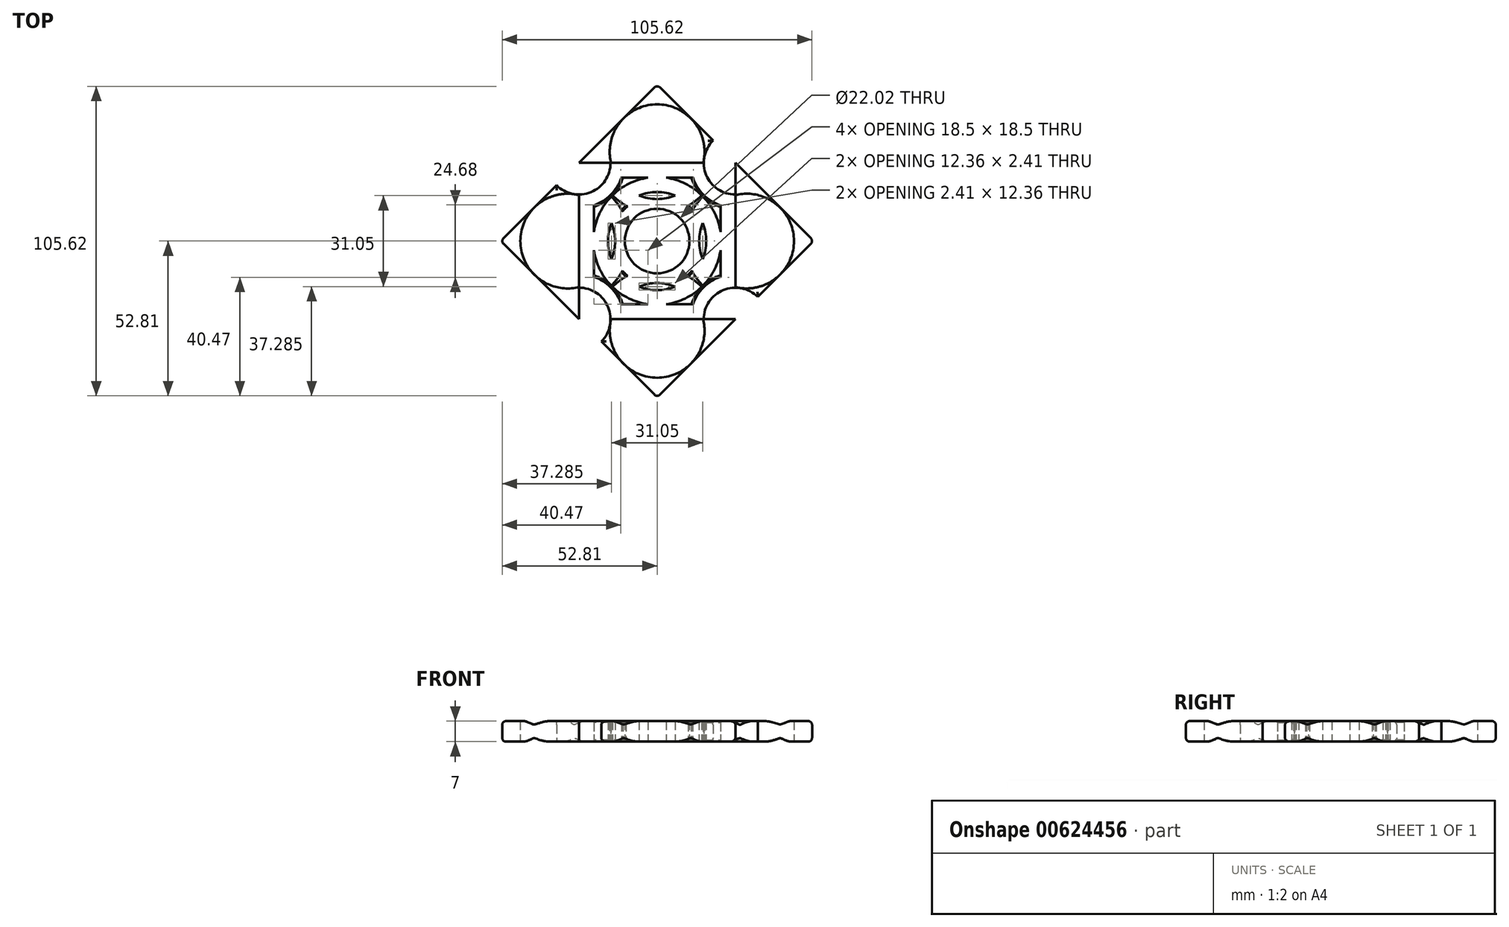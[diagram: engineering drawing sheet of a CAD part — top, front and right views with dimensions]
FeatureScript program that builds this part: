
annotation { "Feature Type Name" : "Feature", "Feature Type Description" : "" }
export const myFeature = defineFeature(function(context is Context, id is Id, definition is map)
    precondition{}
    {
        {
            var Q0;
            Q0=qCreatedBy(makeId("Top.planeOp"),FACE);
            var sketch = newSketch(context, id + "F0", { "sketchPlane" : qUnion([Q0])});
            skCircle(sketch, "E0", {"center": v(0, 0) * mm, "radius": 11.01 * mm});
            skLineSegment(sketch, "E1", {"start": v(0, 0) * mm, "end": v(0, 53.34) * mm});
            skLineSegment(sketch, "E2", {"start": v(0, 0) * mm, "end": v(53.34, 0) * mm});
            skLineSegment(sketch, "E3", {"start": v(0, 0) * mm, "end": v(-53.34, 0) * mm});
            skLineSegment(sketch, "E4", {"start": v(0, 0) * mm, "end": v(0, -53.34) * mm});
            skCircle(sketch, "E5", {"center": v(-30.48, 0) * mm, "radius": 11.01 * mm});
            skCircle(sketch, "E6", {"center": v(0, 30.48) * mm, "radius": 11.01 * mm});
            skCircle(sketch, "E7", {"center": v(30.48, 0) * mm, "radius": 11.01 * mm});
            skCircle(sketch, "E8", {"center": v(0, -30.48) * mm, "radius": 11.01 * mm});
            skLineSegment(sketch, "E9", {"start": v(0, 53.34) * mm, "end": v(-53.34, 0) * mm});
            skLineSegment(sketch, "E10", {"start": v(-53.34, 0) * mm, "end": v(0, -53.34) * mm});
            skLineSegment(sketch, "E11", {"start": v(0, -53.34) * mm, "end": v(53.34, 0) * mm});
            skLineSegment(sketch, "E12", {"start": v(53.34, 0) * mm, "end": v(0, 53.34) * mm});
            skCircle(sketch, "E13", {"center": v(26.67, -26.67) * mm, "radius": 10.78 * mm});
            skCircle(sketch, "E14", {"center": v(-26.67, -26.67) * mm, "radius": 10.78 * mm});
            skCircle(sketch, "E15", {"center": v(-26.67, 26.67) * mm, "radius": 10.78 * mm});
            skCircle(sketch, "E16", {"center": v(26.67, 26.67) * mm, "radius": 10.78 * mm});
            skLineSegment(sketch, "E17", {"start": v(0, 0) * mm, "end": v(-26.67, -26.67) * mm});
            skLineSegment(sketch, "E18", {"start": v(0, 0) * mm, "end": v(26.67, -26.67) * mm});
            skLineSegment(sketch, "E19", {"start": v(0, 0) * mm, "end": v(26.67, 26.67) * mm});
            skLineSegment(sketch, "E20", {"start": v(0, 0) * mm, "end": v(-26.67, 26.67) * mm});
            skLineSegment(sketch, "E21", {"start": v(26.67, 26.67) * mm, "end": v(26.67, -26.67) * mm});
            skLineSegment(sketch, "E22", {"start": v(-26.67, -26.67) * mm, "end": v(26.67, -26.67) * mm});
            skLineSegment(sketch, "E23", {"start": v(-26.67, -26.67) * mm, "end": v(-26.67, 26.67) * mm});
            skLineSegment(sketch, "E24", {"start": v(-26.67, 26.67) * mm, "end": v(26.67, 26.67) * mm});
            skCircle(sketch, "E25", {"center": v(-30.48, 0) * mm, "radius": 16.16 * mm});
            skCircle(sketch, "E26", {"center": v(0, 30.48) * mm, "radius": 16.16 * mm});
            skCircle(sketch, "E27", {"center": v(30.48, 0) * mm, "radius": 16.16 * mm});
            skCircle(sketch, "E28", {"center": v(0, -30.48) * mm, "radius": 16.16 * mm});
            skCircle(sketch, "E29", {"center": v(0, 0) * mm, "radius": 16.73 * mm});
            skSolve(sketch);
        }
        {
            var Q0;
            {var subQ0=sQuery(id+"F0.wireOp",EDGE,"E9");var subQ3=sQuery(id+"F0.wireOp",EDGE,"E26");var subQ5=makeQuery(id+"F0.imprint","INTERSECT",VERTEX,{"derivedFrom":[subQ0,subQ3]});Q0=makeQuery(id+"F0.imprint","IMPRINT",FACE,{"disambiguationData":[TD([[makeQuery(id+"F0.imprint","IMPRINT",EDGE,{"disambiguationData":[TD([[subQ5,1.0]])],"derivedFrom":subQ3}),-1.0]])]});}
            var Q1;
            {var subQ0=sQuery(id+"F0.wireOp",EDGE,"E12");var subQ3=sQuery(id+"F0.wireOp",EDGE,"E26");var subQ5=makeQuery(id+"F0.imprint","INTERSECT",VERTEX,{"derivedFrom":[subQ0,subQ3]});Q1=makeQuery(id+"F0.imprint","IMPRINT",FACE,{"disambiguationData":[TD([[makeQuery(id+"F0.imprint","IMPRINT",EDGE,{"disambiguationData":[TD([[subQ5,-1.0]])],"derivedFrom":subQ3}),-1.0]])]});}
            var Q2;
            {var subQ0=sQuery(id+"F0.wireOp",EDGE,"E11");var subQ3=sQuery(id+"F0.wireOp",EDGE,"E27");var subQ5=makeQuery(id+"F0.imprint","INTERSECT",VERTEX,{"derivedFrom":[subQ0,subQ3]});Q2=makeQuery(id+"F0.imprint","IMPRINT",FACE,{"disambiguationData":[TD([[makeQuery(id+"F0.imprint","IMPRINT",EDGE,{"disambiguationData":[TD([[subQ5,-1.0]])],"derivedFrom":subQ3}),-1.0]])]});}
            var Q3;
            {var subQ0=sQuery(id+"F0.wireOp",EDGE,"E12");var subQ3=sQuery(id+"F0.wireOp",EDGE,"E27");var subQ5=makeQuery(id+"F0.imprint","INTERSECT",VERTEX,{"derivedFrom":[subQ0,subQ3]});Q3=makeQuery(id+"F0.imprint","IMPRINT",FACE,{"disambiguationData":[TD([[makeQuery(id+"F0.imprint","IMPRINT",EDGE,{"disambiguationData":[TD([[subQ5,1.0]])],"derivedFrom":subQ3}),-1.0]])]});}
            var Q4;
            {var subQ0=sQuery(id+"F0.wireOp",EDGE,"E9");var subQ3=sQuery(id+"F0.wireOp",EDGE,"E25");var subQ5=makeQuery(id+"F0.imprint","INTERSECT",VERTEX,{"derivedFrom":[subQ0,subQ3]});Q4=makeQuery(id+"F0.imprint","IMPRINT",FACE,{"disambiguationData":[TD([[makeQuery(id+"F0.imprint","IMPRINT",EDGE,{"disambiguationData":[TD([[subQ5,-1.0]])],"derivedFrom":subQ3}),-1.0]])]});}
            var Q5;
            {var subQ0=sQuery(id+"F0.wireOp",EDGE,"E10");var subQ3=sQuery(id+"F0.wireOp",EDGE,"E25");var subQ5=makeQuery(id+"F0.imprint","INTERSECT",VERTEX,{"derivedFrom":[subQ0,subQ3]});Q5=makeQuery(id+"F0.imprint","IMPRINT",FACE,{"disambiguationData":[TD([[makeQuery(id+"F0.imprint","IMPRINT",EDGE,{"disambiguationData":[TD([[subQ5,1.0]])],"derivedFrom":subQ3}),-1.0]])]});}
            var Q6;
            {var subQ0=sQuery(id+"F0.wireOp",EDGE,"E10");var subQ3=sQuery(id+"F0.wireOp",EDGE,"E28");var subQ5=makeQuery(id+"F0.imprint","INTERSECT",VERTEX,{"derivedFrom":[subQ0,subQ3]});Q6=makeQuery(id+"F0.imprint","IMPRINT",FACE,{"disambiguationData":[TD([[makeQuery(id+"F0.imprint","IMPRINT",EDGE,{"disambiguationData":[TD([[subQ5,-1.0]])],"derivedFrom":subQ3}),-1.0]])]});}
            var Q7;
            {var subQ0=sQuery(id+"F0.wireOp",EDGE,"E11");var subQ3=sQuery(id+"F0.wireOp",EDGE,"E28");var subQ5=makeQuery(id+"F0.imprint","INTERSECT",VERTEX,{"derivedFrom":[subQ0,subQ3]});Q7=makeQuery(id+"F0.imprint","IMPRINT",FACE,{"disambiguationData":[TD([[makeQuery(id+"F0.imprint","IMPRINT",EDGE,{"disambiguationData":[TD([[subQ5,1.0]])],"derivedFrom":subQ3}),-1.0]])]});}
            var Q8;
            {var subQ0=sQuery(id+"F0.wireOp",EDGE,"E26");var subQ1=sQuery(id+"F0.wireOp",EDGE,"E9");var subQ2=makeQuery(id+"F0.imprint","INTERSECT",VERTEX,{"derivedFrom":[subQ1,subQ0]});Q8=makeQuery(id+"F0.imprint","IMPRINT",FACE,{"disambiguationData":[TD([[makeQuery(id+"F0.imprint","IMPRINT",EDGE,{"disambiguationData":[TD([[subQ2,-1.0]])],"derivedFrom":subQ1}),1.0]])]});}
            var Q9;
            {var subQ0=sQuery(id+"F0.wireOp",EDGE,"E15");var subQ1=sQuery(id+"F0.wireOp",EDGE,"E9");var subQ2=makeQuery(id+"F0.imprint","INTERSECT",VERTEX,{"disambiguationData":[OD(1.0)],"derivedFrom":[subQ1,subQ0]});Q9=makeQuery(id+"F0.imprint","IMPRINT",FACE,{"disambiguationData":[TD([[makeQuery(id+"F0.imprint","IMPRINT",EDGE,{"disambiguationData":[TD([[subQ2,-1.0]])],"derivedFrom":subQ1}),1.0]])]});}
            var Q10;
            {var subQ0=sQuery(id+"F0.wireOp",EDGE,"E25");var subQ1=sQuery(id+"F0.wireOp",EDGE,"E10");var subQ2=makeQuery(id+"F0.imprint","INTERSECT",VERTEX,{"derivedFrom":[subQ1,subQ0]});Q10=makeQuery(id+"F0.imprint","IMPRINT",FACE,{"disambiguationData":[TD([[makeQuery(id+"F0.imprint","IMPRINT",EDGE,{"disambiguationData":[TD([[subQ2,-1.0]])],"derivedFrom":subQ1}),1.0]])]});}
            var Q11;
            {var subQ0=sQuery(id+"F0.wireOp",EDGE,"E14");var subQ1=sQuery(id+"F0.wireOp",EDGE,"E10");var subQ2=makeQuery(id+"F0.imprint","INTERSECT",VERTEX,{"disambiguationData":[OD(1.0)],"derivedFrom":[subQ1,subQ0]});Q11=makeQuery(id+"F0.imprint","IMPRINT",FACE,{"disambiguationData":[TD([[makeQuery(id+"F0.imprint","IMPRINT",EDGE,{"disambiguationData":[TD([[subQ2,-1.0]])],"derivedFrom":subQ1}),1.0]])]});}
            var Q12;
            {var subQ0=sQuery(id+"F0.wireOp",EDGE,"E28");var subQ1=sQuery(id+"F0.wireOp",EDGE,"E11");var subQ2=makeQuery(id+"F0.imprint","INTERSECT",VERTEX,{"derivedFrom":[subQ1,subQ0]});Q12=makeQuery(id+"F0.imprint","IMPRINT",FACE,{"disambiguationData":[TD([[makeQuery(id+"F0.imprint","IMPRINT",EDGE,{"disambiguationData":[TD([[subQ2,-1.0]])],"derivedFrom":subQ1}),1.0]])]});}
            var Q13;
            {var subQ0=sQuery(id+"F0.wireOp",EDGE,"E13");var subQ1=sQuery(id+"F0.wireOp",EDGE,"E11");var subQ2=makeQuery(id+"F0.imprint","INTERSECT",VERTEX,{"disambiguationData":[OD(1.0)],"derivedFrom":[subQ1,subQ0]});Q13=makeQuery(id+"F0.imprint","IMPRINT",FACE,{"disambiguationData":[TD([[makeQuery(id+"F0.imprint","IMPRINT",EDGE,{"disambiguationData":[TD([[subQ2,-1.0]])],"derivedFrom":subQ1}),1.0]])]});}
            var Q14;
            {var subQ0=sQuery(id+"F0.wireOp",EDGE,"E27");var subQ1=sQuery(id+"F0.wireOp",EDGE,"E12");var subQ2=makeQuery(id+"F0.imprint","INTERSECT",VERTEX,{"derivedFrom":[subQ1,subQ0]});Q14=makeQuery(id+"F0.imprint","IMPRINT",FACE,{"disambiguationData":[TD([[makeQuery(id+"F0.imprint","IMPRINT",EDGE,{"disambiguationData":[TD([[subQ2,-1.0]])],"derivedFrom":subQ1}),1.0]])]});}
            var Q15;
            {var subQ0=sQuery(id+"F0.wireOp",EDGE,"E16");var subQ1=sQuery(id+"F0.wireOp",EDGE,"E12");var subQ2=makeQuery(id+"F0.imprint","INTERSECT",VERTEX,{"disambiguationData":[OD(1.0)],"derivedFrom":[subQ1,subQ0]});Q15=makeQuery(id+"F0.imprint","IMPRINT",FACE,{"disambiguationData":[TD([[makeQuery(id+"F0.imprint","IMPRINT",EDGE,{"disambiguationData":[TD([[subQ2,-1.0]])],"derivedFrom":subQ1}),1.0]])]});}
            var Q16;
            {var subQ2=sQuery(id+"F0.wireOp",EDGE,"E1");var subQ4=sQuery(id+"F0.wireOp",EDGE,"E6");var subQ5=makeQuery(id+"F0.imprint","INTERSECT",VERTEX,{"disambiguationData":[OD(1.0)],"derivedFrom":[subQ2,subQ4]});Q16=makeQuery(id+"F0.imprint","IMPRINT",FACE,{"disambiguationData":[TD([[makeQuery(id+"F0.imprint","IMPRINT",EDGE,{"disambiguationData":[TD([[subQ5,-1.0]])],"derivedFrom":subQ2}),1.0]])]});}
            var Q17;
            {var subQ2=sQuery(id+"F0.wireOp",EDGE,"E1");var subQ5=sQuery(id+"F0.wireOp",EDGE,"E6");var subQ8=makeQuery(id+"F0.imprint","INTERSECT",VERTEX,{"disambiguationData":[OD(1.0)],"derivedFrom":[subQ2,subQ5]});Q17=makeQuery(id+"F0.imprint","IMPRINT",FACE,{"disambiguationData":[TD([[makeQuery(id+"F0.imprint","IMPRINT",EDGE,{"disambiguationData":[TD([[subQ8,-1.0]])],"derivedFrom":subQ2}),-1.0]])]});}
            var Q18;
            {var subQ2=sQuery(id+"F0.wireOp",EDGE,"E2");var subQ5=sQuery(id+"F0.wireOp",EDGE,"E7");var subQ8=makeQuery(id+"F0.imprint","INTERSECT",VERTEX,{"disambiguationData":[OD(1.0)],"derivedFrom":[subQ2,subQ5]});Q18=makeQuery(id+"F0.imprint","IMPRINT",FACE,{"disambiguationData":[TD([[makeQuery(id+"F0.imprint","IMPRINT",EDGE,{"disambiguationData":[TD([[subQ8,-1.0]])],"derivedFrom":subQ2}),1.0]])]});}
            var Q19;
            {var subQ4=sQuery(id+"F0.wireOp",EDGE,"E7");var subQ6=sQuery(id+"F0.wireOp",EDGE,"E2");var subQ7=makeQuery(id+"F0.imprint","INTERSECT",VERTEX,{"disambiguationData":[OD(1.0)],"derivedFrom":[subQ6,subQ4]});Q19=makeQuery(id+"F0.imprint","IMPRINT",FACE,{"disambiguationData":[TD([[makeQuery(id+"F0.imprint","IMPRINT",EDGE,{"disambiguationData":[TD([[subQ7,-1.0]])],"derivedFrom":subQ6}),-1.0]])]});}
            var Q20;
            {var subQ1=sQuery(id+"F0.wireOp",EDGE,"E5");var subQ5=sQuery(id+"F0.wireOp",EDGE,"E3");var subQ6=makeQuery(id+"F0.imprint","INTERSECT",VERTEX,{"disambiguationData":[OD(1.0)],"derivedFrom":[subQ5,subQ1]});Q20=makeQuery(id+"F0.imprint","IMPRINT",FACE,{"disambiguationData":[TD([[makeQuery(id+"F0.imprint","IMPRINT",EDGE,{"disambiguationData":[TD([[subQ6,-1.0]])],"derivedFrom":subQ5}),-1.0]])]});}
            var Q21;
            {var subQ1=sQuery(id+"F0.wireOp",EDGE,"E5");var subQ6=sQuery(id+"F0.wireOp",EDGE,"E3");var subQ8=makeQuery(id+"F0.imprint","INTERSECT",VERTEX,{"disambiguationData":[OD(1.0)],"derivedFrom":[subQ6,subQ1]});Q21=makeQuery(id+"F0.imprint","IMPRINT",FACE,{"disambiguationData":[TD([[makeQuery(id+"F0.imprint","IMPRINT",EDGE,{"disambiguationData":[TD([[subQ8,-1.0]])],"derivedFrom":subQ6}),1.0]])]});}
            var Q22;
            {var subQ4=sQuery(id+"F0.wireOp",EDGE,"E8");var subQ6=sQuery(id+"F0.wireOp",EDGE,"E4");var subQ7=makeQuery(id+"F0.imprint","INTERSECT",VERTEX,{"disambiguationData":[OD(1.0)],"derivedFrom":[subQ6,subQ4]});Q22=makeQuery(id+"F0.imprint","IMPRINT",FACE,{"disambiguationData":[TD([[makeQuery(id+"F0.imprint","IMPRINT",EDGE,{"disambiguationData":[TD([[subQ7,-1.0]])],"derivedFrom":subQ6}),-1.0]])]});}
            var Q23;
            {var subQ1=sQuery(id+"F0.wireOp",EDGE,"E8");var subQ5=sQuery(id+"F0.wireOp",EDGE,"E4");var subQ6=makeQuery(id+"F0.imprint","INTERSECT",VERTEX,{"disambiguationData":[OD(1.0)],"derivedFrom":[subQ5,subQ1]});Q23=makeQuery(id+"F0.imprint","IMPRINT",FACE,{"disambiguationData":[TD([[makeQuery(id+"F0.imprint","IMPRINT",EDGE,{"disambiguationData":[TD([[subQ6,-1.0]])],"derivedFrom":subQ5}),1.0]])]});}
            var Q24;
            {var subQ3=sQuery(id+"F0.wireOp",EDGE,"E29");var subQ6=sQuery(id+"F0.wireOp",EDGE,"E3");var subQ9=makeQuery(id+"F0.imprint","INTERSECT",VERTEX,{"derivedFrom":[subQ6,subQ3]});Q24=makeQuery(id+"F0.imprint","IMPRINT",FACE,{"disambiguationData":[TD([[makeQuery(id+"F0.imprint","IMPRINT",EDGE,{"disambiguationData":[TD([[subQ9,-1.0]])],"derivedFrom":subQ6}),-1.0]])]});}
            var Q25;
            {var subQ3=sQuery(id+"F0.wireOp",EDGE,"E29");var subQ7=sQuery(id+"F0.wireOp",EDGE,"E1");var subQ9=makeQuery(id+"F0.imprint","INTERSECT",VERTEX,{"derivedFrom":[subQ7,subQ3]});Q25=makeQuery(id+"F0.imprint","IMPRINT",FACE,{"disambiguationData":[TD([[makeQuery(id+"F0.imprint","IMPRINT",EDGE,{"disambiguationData":[TD([[subQ9,-1.0]])],"derivedFrom":subQ7}),1.0]])]});}
            var Q26;
            {var subQ3=sQuery(id+"F0.wireOp",EDGE,"E29");var subQ7=sQuery(id+"F0.wireOp",EDGE,"E1");var subQ9=makeQuery(id+"F0.imprint","INTERSECT",VERTEX,{"derivedFrom":[subQ7,subQ3]});Q26=makeQuery(id+"F0.imprint","IMPRINT",FACE,{"disambiguationData":[TD([[makeQuery(id+"F0.imprint","IMPRINT",EDGE,{"disambiguationData":[TD([[subQ9,-1.0]])],"derivedFrom":subQ7}),-1.0]])]});}
            var Q27;
            {var subQ3=sQuery(id+"F0.wireOp",EDGE,"E29");var subQ7=sQuery(id+"F0.wireOp",EDGE,"E2");var subQ8=makeQuery(id+"F0.imprint","INTERSECT",VERTEX,{"derivedFrom":[subQ7,subQ3]});Q27=makeQuery(id+"F0.imprint","IMPRINT",FACE,{"disambiguationData":[TD([[makeQuery(id+"F0.imprint","IMPRINT",EDGE,{"disambiguationData":[TD([[subQ8,-1.0]])],"derivedFrom":subQ7}),1.0]])]});}
            var Q28;
            {var subQ5=sQuery(id+"F0.wireOp",EDGE,"E2");var subQ7=sQuery(id+"F0.wireOp",EDGE,"E29");var subQ9=makeQuery(id+"F0.imprint","INTERSECT",VERTEX,{"derivedFrom":[subQ5,subQ7]});Q28=makeQuery(id+"F0.imprint","IMPRINT",FACE,{"disambiguationData":[TD([[makeQuery(id+"F0.imprint","IMPRINT",EDGE,{"disambiguationData":[TD([[subQ9,-1.0]])],"derivedFrom":subQ5}),-1.0]])]});}
            var Q29;
            {var subQ5=sQuery(id+"F0.wireOp",EDGE,"E4");var subQ7=sQuery(id+"F0.wireOp",EDGE,"E29");var subQ9=makeQuery(id+"F0.imprint","INTERSECT",VERTEX,{"derivedFrom":[subQ5,subQ7]});Q29=makeQuery(id+"F0.imprint","IMPRINT",FACE,{"disambiguationData":[TD([[makeQuery(id+"F0.imprint","IMPRINT",EDGE,{"disambiguationData":[TD([[subQ9,-1.0]])],"derivedFrom":subQ5}),1.0]])]});}
            var Q30;
            {var subQ5=sQuery(id+"F0.wireOp",EDGE,"E4");var subQ7=sQuery(id+"F0.wireOp",EDGE,"E29");var subQ9=makeQuery(id+"F0.imprint","INTERSECT",VERTEX,{"derivedFrom":[subQ5,subQ7]});Q30=makeQuery(id+"F0.imprint","IMPRINT",FACE,{"disambiguationData":[TD([[makeQuery(id+"F0.imprint","IMPRINT",EDGE,{"disambiguationData":[TD([[subQ9,-1.0]])],"derivedFrom":subQ5}),-1.0]])]});}
            var Q31;
            {var subQ0=sQuery(id+"F0.wireOp",EDGE,"E17");var subQ1=sQuery(id+"F0.wireOp",EDGE,"E14");var subQ2=makeQuery(id+"F0.imprint","INTERSECT",VERTEX,{"derivedFrom":[subQ1,subQ0]});Q31=makeQuery(id+"F0.imprint","IMPRINT",FACE,{"disambiguationData":[TD([[makeQuery(id+"F0.imprint","IMPRINT",EDGE,{"disambiguationData":[TD([[subQ2,1.0]])],"derivedFrom":subQ1}),-1.0]])]});}
            var Q32;
            {var subQ5=sQuery(id+"F0.wireOp",EDGE,"E14");var subQ7=sQuery(id+"F0.wireOp",EDGE,"E17");var subQ8=makeQuery(id+"F0.imprint","INTERSECT",VERTEX,{"derivedFrom":[subQ5,subQ7]});Q32=makeQuery(id+"F0.imprint","IMPRINT",FACE,{"disambiguationData":[TD([[makeQuery(id+"F0.imprint","IMPRINT",EDGE,{"disambiguationData":[TD([[subQ8,-1.0]])],"derivedFrom":subQ5}),-1.0]])]});}
            var Q33;
            {var subQ1=sQuery(id+"F0.wireOp",EDGE,"E13");var subQ5=sQuery(id+"F0.wireOp",EDGE,"E18");var subQ6=makeQuery(id+"F0.imprint","INTERSECT",VERTEX,{"derivedFrom":[subQ1,subQ5]});Q33=makeQuery(id+"F0.imprint","IMPRINT",FACE,{"disambiguationData":[TD([[makeQuery(id+"F0.imprint","IMPRINT",EDGE,{"disambiguationData":[TD([[subQ6,-1.0]])],"derivedFrom":subQ1}),-1.0]])]});}
            var Q34;
            {var subQ1=sQuery(id+"F0.wireOp",EDGE,"E24");var subQ5=sQuery(id+"F0.wireOp",EDGE,"E16");var subQ6=makeQuery(id+"F0.imprint","INTERSECT",VERTEX,{"derivedFrom":[subQ5,subQ1]});Q34=makeQuery(id+"F0.imprint","IMPRINT",FACE,{"disambiguationData":[TD([[makeQuery(id+"F0.imprint","IMPRINT",EDGE,{"disambiguationData":[TD([[subQ6,-1.0]])],"derivedFrom":subQ5}),-1.0]])]});}
            var Q35;
            {var subQ5=sQuery(id+"F0.wireOp",EDGE,"E19");var subQ6=sQuery(id+"F0.wireOp",EDGE,"E16");var subQ7=makeQuery(id+"F0.imprint","INTERSECT",VERTEX,{"derivedFrom":[subQ6,subQ5]});Q35=makeQuery(id+"F0.imprint","IMPRINT",FACE,{"disambiguationData":[TD([[makeQuery(id+"F0.imprint","IMPRINT",EDGE,{"disambiguationData":[TD([[subQ7,-1.0]])],"derivedFrom":subQ6}),-1.0]])]});}
            var Q36;
            {var subQ0=sQuery(id+"F0.wireOp",EDGE,"E24");var subQ1=sQuery(id+"F0.wireOp",EDGE,"E15");var subQ2=makeQuery(id+"F0.imprint","INTERSECT",VERTEX,{"derivedFrom":[subQ1,subQ0]});Q36=makeQuery(id+"F0.imprint","IMPRINT",FACE,{"disambiguationData":[TD([[makeQuery(id+"F0.imprint","IMPRINT",EDGE,{"disambiguationData":[TD([[subQ2,1.0]])],"derivedFrom":subQ1}),-1.0]])]});}
            var Q37;
            {var subQ3=sQuery(id+"F0.wireOp",EDGE,"E29");var subQ7=sQuery(id+"F0.wireOp",EDGE,"E3");var subQ9=makeQuery(id+"F0.imprint","INTERSECT",VERTEX,{"derivedFrom":[subQ7,subQ3]});Q37=makeQuery(id+"F0.imprint","IMPRINT",FACE,{"disambiguationData":[TD([[makeQuery(id+"F0.imprint","IMPRINT",EDGE,{"disambiguationData":[TD([[subQ9,-1.0]])],"derivedFrom":subQ7}),1.0]])]});}
            var Q38;
            {var subQ1=sQuery(id+"F0.wireOp",EDGE,"E23");var subQ5=sQuery(id+"F0.wireOp",EDGE,"E15");var subQ6=makeQuery(id+"F0.imprint","INTERSECT",VERTEX,{"derivedFrom":[subQ5,subQ1]});Q38=makeQuery(id+"F0.imprint","IMPRINT",FACE,{"disambiguationData":[TD([[makeQuery(id+"F0.imprint","IMPRINT",EDGE,{"disambiguationData":[TD([[subQ6,-1.0]])],"derivedFrom":subQ5}),-1.0]])]});}
            var Q39;
            {var subQ1=sQuery(id+"F0.wireOp",EDGE,"E21");var subQ5=sQuery(id+"F0.wireOp",EDGE,"E13");var subQ6=makeQuery(id+"F0.imprint","INTERSECT",VERTEX,{"derivedFrom":[subQ5,subQ1]});Q39=makeQuery(id+"F0.imprint","IMPRINT",FACE,{"disambiguationData":[TD([[makeQuery(id+"F0.imprint","IMPRINT",EDGE,{"disambiguationData":[TD([[subQ6,-1.0]])],"derivedFrom":subQ5}),-1.0]])]});}
            var Q40;
            {var subQ1=sQuery(id+"F0.wireOp",EDGE,"E2");var subQ6=sQuery(id+"F0.wireOp",EDGE,"E0");var subQ9=makeQuery(id+"F0.imprint","INTERSECT",VERTEX,{"derivedFrom":[subQ6,subQ1]});Q40=makeQuery(id+"F0.imprint","IMPRINT",FACE,{"disambiguationData":[TD([[makeQuery(id+"F0.imprint","IMPRINT",EDGE,{"disambiguationData":[TD([[subQ9,1.0]])],"derivedFrom":subQ6}),-1.0]])]});}
            var Q41;
            {var subQ1=sQuery(id+"F0.wireOp",EDGE,"E0");var subQ5=sQuery(id+"F0.wireOp",EDGE,"E4");var subQ6=makeQuery(id+"F0.imprint","INTERSECT",VERTEX,{"derivedFrom":[subQ1,subQ5]});Q41=makeQuery(id+"F0.imprint","IMPRINT",FACE,{"disambiguationData":[TD([[makeQuery(id+"F0.imprint","IMPRINT",EDGE,{"disambiguationData":[TD([[subQ6,-1.0]])],"derivedFrom":subQ1}),-1.0]])]});}
            var Q42;
            {var subQ5=sQuery(id+"F0.wireOp",EDGE,"E17");var subQ6=sQuery(id+"F0.wireOp",EDGE,"E0");var subQ7=makeQuery(id+"F0.imprint","INTERSECT",VERTEX,{"derivedFrom":[subQ6,subQ5]});Q42=makeQuery(id+"F0.imprint","IMPRINT",FACE,{"disambiguationData":[TD([[makeQuery(id+"F0.imprint","IMPRINT",EDGE,{"disambiguationData":[TD([[subQ7,-1.0]])],"derivedFrom":subQ6}),-1.0]])]});}
            var Q43;
            {var subQ1=sQuery(id+"F0.wireOp",EDGE,"E0");var subQ7=sQuery(id+"F0.wireOp",EDGE,"E3");var subQ9=makeQuery(id+"F0.imprint","INTERSECT",VERTEX,{"derivedFrom":[subQ1,subQ7]});Q43=makeQuery(id+"F0.imprint","IMPRINT",FACE,{"disambiguationData":[TD([[makeQuery(id+"F0.imprint","IMPRINT",EDGE,{"disambiguationData":[TD([[subQ9,-1.0]])],"derivedFrom":subQ1}),-1.0]])]});}
            var Q44;
            {var subQ1=sQuery(id+"F0.wireOp",EDGE,"E1");var subQ6=sQuery(id+"F0.wireOp",EDGE,"E0");var subQ9=makeQuery(id+"F0.imprint","INTERSECT",VERTEX,{"derivedFrom":[subQ6,subQ1]});Q44=makeQuery(id+"F0.imprint","IMPRINT",FACE,{"disambiguationData":[TD([[makeQuery(id+"F0.imprint","IMPRINT",EDGE,{"disambiguationData":[TD([[subQ9,-1.0]])],"derivedFrom":subQ6}),-1.0]])]});}
            var Q45;
            {var subQ0=sQuery(id+"F0.wireOp",EDGE,"E19");var subQ1=sQuery(id+"F0.wireOp",EDGE,"E0");var subQ2=makeQuery(id+"F0.imprint","INTERSECT",VERTEX,{"derivedFrom":[subQ1,subQ0]});Q45=makeQuery(id+"F0.imprint","IMPRINT",FACE,{"disambiguationData":[TD([[makeQuery(id+"F0.imprint","IMPRINT",EDGE,{"disambiguationData":[TD([[subQ2,-1.0]])],"derivedFrom":subQ1}),-1.0]])]});}
            var Q46;
            {var subQ0=sQuery(id+"F0.wireOp",EDGE,"E28");var subQ1=sQuery(id+"F0.wireOp",EDGE,"E4");var subQ2=makeQuery(id+"F0.imprint","INTERSECT",VERTEX,{"disambiguationData":[OD(0.0)],"derivedFrom":[subQ1,subQ0]});Q46=makeQuery(id+"F0.imprint","IMPRINT",FACE,{"disambiguationData":[TD([[makeQuery(id+"F0.imprint","IMPRINT",EDGE,{"disambiguationData":[TD([[subQ2,-1.0]])],"derivedFrom":subQ1}),1.0]])]});}
            var Q47;
            {var subQ0=sQuery(id+"F0.wireOp",EDGE,"E28");var subQ1=sQuery(id+"F0.wireOp",EDGE,"E4");var subQ2=makeQuery(id+"F0.imprint","INTERSECT",VERTEX,{"disambiguationData":[OD(0.0)],"derivedFrom":[subQ1,subQ0]});Q47=makeQuery(id+"F0.imprint","IMPRINT",FACE,{"disambiguationData":[TD([[makeQuery(id+"F0.imprint","IMPRINT",EDGE,{"disambiguationData":[TD([[subQ2,-1.0]])],"derivedFrom":subQ1}),-1.0]])]});}
            var Q48;
            {var subQ0=sQuery(id+"F0.wireOp",EDGE,"E27");var subQ1=sQuery(id+"F0.wireOp",EDGE,"E2");var subQ2=makeQuery(id+"F0.imprint","INTERSECT",VERTEX,{"disambiguationData":[OD(0.0)],"derivedFrom":[subQ1,subQ0]});Q48=makeQuery(id+"F0.imprint","IMPRINT",FACE,{"disambiguationData":[TD([[makeQuery(id+"F0.imprint","IMPRINT",EDGE,{"disambiguationData":[TD([[subQ2,-1.0]])],"derivedFrom":subQ1}),-1.0]])]});}
            var Q49;
            {var subQ0=sQuery(id+"F0.wireOp",EDGE,"E27");var subQ1=sQuery(id+"F0.wireOp",EDGE,"E2");var subQ2=makeQuery(id+"F0.imprint","INTERSECT",VERTEX,{"disambiguationData":[OD(0.0)],"derivedFrom":[subQ1,subQ0]});Q49=makeQuery(id+"F0.imprint","IMPRINT",FACE,{"disambiguationData":[TD([[makeQuery(id+"F0.imprint","IMPRINT",EDGE,{"disambiguationData":[TD([[subQ2,-1.0]])],"derivedFrom":subQ1}),1.0]])]});}
            var Q50;
            {var subQ0=sQuery(id+"F0.wireOp",EDGE,"E19");var subQ1=sQuery(id+"F0.wireOp",EDGE,"E0");var subQ2=makeQuery(id+"F0.imprint","INTERSECT",VERTEX,{"derivedFrom":[subQ1,subQ0]});Q50=makeQuery(id+"F0.imprint","IMPRINT",FACE,{"disambiguationData":[TD([[makeQuery(id+"F0.imprint","IMPRINT",EDGE,{"disambiguationData":[TD([[subQ2,1.0]])],"derivedFrom":subQ1}),-1.0]])]});}
            var Q51;
            {var subQ0=sQuery(id+"F0.wireOp",EDGE,"E26");var subQ1=sQuery(id+"F0.wireOp",EDGE,"E1");var subQ2=makeQuery(id+"F0.imprint","INTERSECT",VERTEX,{"disambiguationData":[OD(0.0)],"derivedFrom":[subQ1,subQ0]});Q51=makeQuery(id+"F0.imprint","IMPRINT",FACE,{"disambiguationData":[TD([[makeQuery(id+"F0.imprint","IMPRINT",EDGE,{"disambiguationData":[TD([[subQ2,-1.0]])],"derivedFrom":subQ1}),-1.0]])]});}
            var Q52;
            {var subQ0=sQuery(id+"F0.wireOp",EDGE,"E26");var subQ1=sQuery(id+"F0.wireOp",EDGE,"E1");var subQ2=makeQuery(id+"F0.imprint","INTERSECT",VERTEX,{"disambiguationData":[OD(0.0)],"derivedFrom":[subQ1,subQ0]});Q52=makeQuery(id+"F0.imprint","IMPRINT",FACE,{"disambiguationData":[TD([[makeQuery(id+"F0.imprint","IMPRINT",EDGE,{"disambiguationData":[TD([[subQ2,-1.0]])],"derivedFrom":subQ1}),1.0]])]});}
            var Q53;
            {var subQ1=sQuery(id+"F0.wireOp",EDGE,"E0");var subQ5=sQuery(id+"F0.wireOp",EDGE,"E20");var subQ6=makeQuery(id+"F0.imprint","INTERSECT",VERTEX,{"derivedFrom":[subQ1,subQ5]});Q53=makeQuery(id+"F0.imprint","IMPRINT",FACE,{"disambiguationData":[TD([[makeQuery(id+"F0.imprint","IMPRINT",EDGE,{"disambiguationData":[TD([[subQ6,-1.0]])],"derivedFrom":subQ1}),-1.0]])]});}
            var Q54;
            {var subQ0=sQuery(id+"F0.wireOp",EDGE,"E25");var subQ1=sQuery(id+"F0.wireOp",EDGE,"E3");var subQ2=makeQuery(id+"F0.imprint","INTERSECT",VERTEX,{"disambiguationData":[OD(0.0)],"derivedFrom":[subQ1,subQ0]});Q54=makeQuery(id+"F0.imprint","IMPRINT",FACE,{"disambiguationData":[TD([[makeQuery(id+"F0.imprint","IMPRINT",EDGE,{"disambiguationData":[TD([[subQ2,-1.0]])],"derivedFrom":subQ1}),-1.0]])]});}
            var Q55;
            {var subQ0=sQuery(id+"F0.wireOp",EDGE,"E25");var subQ1=sQuery(id+"F0.wireOp",EDGE,"E3");var subQ2=makeQuery(id+"F0.imprint","INTERSECT",VERTEX,{"disambiguationData":[OD(0.0)],"derivedFrom":[subQ1,subQ0]});Q55=makeQuery(id+"F0.imprint","IMPRINT",FACE,{"disambiguationData":[TD([[makeQuery(id+"F0.imprint","IMPRINT",EDGE,{"disambiguationData":[TD([[subQ2,-1.0]])],"derivedFrom":subQ1}),1.0]])]});}
            extrude(context, id + "F1", {"entities" : qUnion([Q0, Q1, Q2, Q3, Q4, Q5, Q6, Q7, Q8, Q9, Q10, Q11, Q12, Q13, Q14, Q15, Q16, Q17, Q18, Q19, Q20, Q21, Q22, Q23, Q24, Q25, Q26, Q27, Q28, Q29, Q30, Q31, Q32, Q33, Q34, Q35, Q36, Q37, Q38, Q39, Q40, Q41, Q42, Q43, Q44, Q45, Q46, Q47, Q48, Q49, Q50, Q51, Q52, Q53, Q54, Q55]), "depth" : 7 * mm, "offsetDistance" : 25.4 * mm});
        }
        {
            var Q0;
            Q0=makeQuery(id+"F1.opExtrude","CAP_FACE",FACE,{"disambiguationData":[OSD([sQuery(id+"F0.wireOp",EDGE,"E0"),sQuery(id+"F0.wireOp",EDGE,"E5"),sQuery(id+"F0.wireOp",EDGE,"E6"),sQuery(id+"F0.wireOp",EDGE,"E7"),sQuery(id+"F0.wireOp",EDGE,"E8"),sQuery(id+"F0.wireOp",EDGE,"E9"),sQuery(id+"F0.wireOp",EDGE,"E10"),sQuery(id+"F0.wireOp",EDGE,"E11"),sQuery(id+"F0.wireOp",EDGE,"E12"),sQuery(id+"F0.wireOp",EDGE,"E13"),sQuery(id+"F0.wireOp",EDGE,"E14"),sQuery(id+"F0.wireOp",EDGE,"E15"),sQuery(id+"F0.wireOp",EDGE,"E16")])],"isStart":false});
            var Q1;
            Q1=makeQuery(id+"F1.opExtrude","CAP_FACE",FACE,{"disambiguationData":[OSD([sQuery(id+"F0.wireOp",EDGE,"E0"),sQuery(id+"F0.wireOp",EDGE,"E5"),sQuery(id+"F0.wireOp",EDGE,"E6"),sQuery(id+"F0.wireOp",EDGE,"E7"),sQuery(id+"F0.wireOp",EDGE,"E8"),sQuery(id+"F0.wireOp",EDGE,"E9"),sQuery(id+"F0.wireOp",EDGE,"E10"),sQuery(id+"F0.wireOp",EDGE,"E11"),sQuery(id+"F0.wireOp",EDGE,"E12"),sQuery(id+"F0.wireOp",EDGE,"E13"),sQuery(id+"F0.wireOp",EDGE,"E14"),sQuery(id+"F0.wireOp",EDGE,"E15"),sQuery(id+"F0.wireOp",EDGE,"E16")])],"isStart":true});
            shell(context, id + "F2", {"entities" : qUnion([Q0, Q1]), "thickness" : 5.08 * mm});
        }
        {
            var Q0;
            Q0=makeQuery(id+"F1.opExtrude","SWEPT_EDGE",EDGE,{"disambiguationData":[OSD([sQuery(id+"F0.wireOp",EDGE,"E4"),sQuery(id+"F0.wireOp",EDGE,"E10"),sQuery(id+"F0.wireOp",EDGE,"E11")])]});
            var Q1;
            Q1=makeQuery(id+"F1.opExtrude","SWEPT_EDGE",EDGE,{"disambiguationData":[OSD([sQuery(id+"F0.wireOp",EDGE,"E3"),sQuery(id+"F0.wireOp",EDGE,"E9"),sQuery(id+"F0.wireOp",EDGE,"E10")])]});
            var Q2;
            Q2=makeQuery(id+"F1.opExtrude","SWEPT_EDGE",EDGE,{"disambiguationData":[OSD([sQuery(id+"F0.wireOp",EDGE,"E1"),sQuery(id+"F0.wireOp",EDGE,"E9"),sQuery(id+"F0.wireOp",EDGE,"E12")])]});
            var Q3;
            Q3=makeQuery(id+"F1.opExtrude","SWEPT_EDGE",EDGE,{"disambiguationData":[OSD([sQuery(id+"F0.wireOp",EDGE,"E2"),sQuery(id+"F0.wireOp",EDGE,"E11"),sQuery(id+"F0.wireOp",EDGE,"E12")])]});
            fillet(context, id + "F3", {"entities" : qUnion([Q0, Q1, Q2, Q3]), "radius" : 1.27 * mm, "tangentPropagation" : true, "allowEdgeOverflow" : false});
        }
        {
            var Q0;
            {var subQ0=sQuery(id+"F0.wireOp",EDGE,"E10");var subQ1=makeQuery(id+"F0.imprint","INTERSECT",VERTEX,{"derivedFrom":[subQ0,sQuery(id+"F0.wireOp",EDGE,"E25")]});Q0=makeQuery(id+"F1.opExtrude","CAP_EDGE",EDGE,{"disambiguationData":[OSD([subQ0]),TDD([makeQuery(id+"F0.imprint","IMPRINT",EDGE,{"disambiguationData":[TD([[subQ1,1.0]])],"derivedFrom":subQ0}),makeQuery(id+"F0.imprint","IMPRINT",EDGE,{"disambiguationData":[TD([[subQ1,-1.0]])],"derivedFrom":subQ0})])],"isStart":false});}
            var Q1;
            {var subQ0=sQuery(id+"F0.wireOp",EDGE,"E9");var subQ1=makeQuery(id+"F0.imprint","INTERSECT",VERTEX,{"derivedFrom":[subQ0,sQuery(id+"F0.wireOp",EDGE,"E25")]});Q1=makeQuery(id+"F1.opExtrude","CAP_EDGE",EDGE,{"disambiguationData":[OSD([subQ0]),TDD([makeQuery(id+"F0.imprint","IMPRINT",EDGE,{"disambiguationData":[TD([[makeQuery(id+"F0.imprint","INTERSECT",VERTEX,{"disambiguationData":[OD(1.0)],"derivedFrom":[subQ0,sQuery(id+"F0.wireOp",EDGE,"E15")]}),-1.0]])],"derivedFrom":subQ0}),makeQuery(id+"F0.imprint","IMPRINT",EDGE,{"disambiguationData":[TD([[subQ1,-1.0]])],"derivedFrom":subQ0})])],"isStart":false});}
            var Q2;
            {var subQ0=sQuery(id+"F0.wireOp",EDGE,"E10");var subQ1=makeQuery(id+"F0.imprint","INTERSECT",VERTEX,{"derivedFrom":[subQ0,sQuery(id+"F0.wireOp",EDGE,"E28")]});Q2=makeQuery(id+"F1.opExtrude","CAP_EDGE",EDGE,{"disambiguationData":[OSD([subQ0]),TDD([makeQuery(id+"F0.imprint","IMPRINT",EDGE,{"disambiguationData":[TD([[makeQuery(id+"F0.imprint","INTERSECT",VERTEX,{"disambiguationData":[OD(1.0)],"derivedFrom":[subQ0,sQuery(id+"F0.wireOp",EDGE,"E14")]}),-1.0]])],"derivedFrom":subQ0}),makeQuery(id+"F0.imprint","IMPRINT",EDGE,{"disambiguationData":[TD([[subQ1,-1.0]])],"derivedFrom":subQ0})])],"isStart":false});}
            var Q3;
            {var subQ0=sQuery(id+"F0.wireOp",EDGE,"E11");var subQ1=makeQuery(id+"F0.imprint","INTERSECT",VERTEX,{"derivedFrom":[subQ0,sQuery(id+"F0.wireOp",EDGE,"E28")]});Q3=makeQuery(id+"F1.opExtrude","CAP_EDGE",EDGE,{"disambiguationData":[OSD([subQ0]),TDD([makeQuery(id+"F0.imprint","IMPRINT",EDGE,{"disambiguationData":[TD([[subQ1,1.0]])],"derivedFrom":subQ0}),makeQuery(id+"F0.imprint","IMPRINT",EDGE,{"disambiguationData":[TD([[subQ1,-1.0]])],"derivedFrom":subQ0})])],"isStart":false});}
            var Q4;
            {var subQ0=sQuery(id+"F0.wireOp",EDGE,"E11");var subQ1=makeQuery(id+"F0.imprint","INTERSECT",VERTEX,{"derivedFrom":[subQ0,sQuery(id+"F0.wireOp",EDGE,"E27")]});Q4=makeQuery(id+"F1.opExtrude","CAP_EDGE",EDGE,{"disambiguationData":[OSD([subQ0]),TDD([makeQuery(id+"F0.imprint","IMPRINT",EDGE,{"disambiguationData":[TD([[makeQuery(id+"F0.imprint","INTERSECT",VERTEX,{"disambiguationData":[OD(1.0)],"derivedFrom":[subQ0,sQuery(id+"F0.wireOp",EDGE,"E13")]}),-1.0]])],"derivedFrom":subQ0}),makeQuery(id+"F0.imprint","IMPRINT",EDGE,{"disambiguationData":[TD([[subQ1,-1.0]])],"derivedFrom":subQ0})])],"isStart":false});}
            var Q5;
            {var subQ0=sQuery(id+"F0.wireOp",EDGE,"E12");var subQ1=makeQuery(id+"F0.imprint","INTERSECT",VERTEX,{"derivedFrom":[subQ0,sQuery(id+"F0.wireOp",EDGE,"E27")]});Q5=makeQuery(id+"F1.opExtrude","CAP_EDGE",EDGE,{"disambiguationData":[OSD([subQ0]),TDD([makeQuery(id+"F0.imprint","IMPRINT",EDGE,{"disambiguationData":[TD([[subQ1,1.0]])],"derivedFrom":subQ0}),makeQuery(id+"F0.imprint","IMPRINT",EDGE,{"disambiguationData":[TD([[subQ1,-1.0]])],"derivedFrom":subQ0})])],"isStart":false});}
            var Q6;
            {var subQ0=sQuery(id+"F0.wireOp",EDGE,"E12");var subQ1=makeQuery(id+"F0.imprint","INTERSECT",VERTEX,{"derivedFrom":[subQ0,sQuery(id+"F0.wireOp",EDGE,"E26")]});Q6=makeQuery(id+"F1.opExtrude","CAP_EDGE",EDGE,{"disambiguationData":[OSD([subQ0]),TDD([makeQuery(id+"F0.imprint","IMPRINT",EDGE,{"disambiguationData":[TD([[makeQuery(id+"F0.imprint","INTERSECT",VERTEX,{"disambiguationData":[OD(1.0)],"derivedFrom":[subQ0,sQuery(id+"F0.wireOp",EDGE,"E16")]}),-1.0]])],"derivedFrom":subQ0}),makeQuery(id+"F0.imprint","IMPRINT",EDGE,{"disambiguationData":[TD([[subQ1,-1.0]])],"derivedFrom":subQ0})])],"isStart":false});}
            var Q7;
            {var subQ0=sQuery(id+"F0.wireOp",EDGE,"E9");var subQ1=makeQuery(id+"F0.imprint","INTERSECT",VERTEX,{"derivedFrom":[subQ0,sQuery(id+"F0.wireOp",EDGE,"E26")]});Q7=makeQuery(id+"F1.opExtrude","CAP_EDGE",EDGE,{"disambiguationData":[OSD([subQ0]),TDD([makeQuery(id+"F0.imprint","IMPRINT",EDGE,{"disambiguationData":[TD([[subQ1,1.0]])],"derivedFrom":subQ0}),makeQuery(id+"F0.imprint","IMPRINT",EDGE,{"disambiguationData":[TD([[subQ1,-1.0]])],"derivedFrom":subQ0})])],"isStart":false});}
            var Q8;
            {var subQ0=sQuery(id+"F0.wireOp",EDGE,"E14");var subQ1=makeQuery(id+"F0.imprint","INTERSECT",VERTEX,{"derivedFrom":[subQ0,sQuery(id+"F0.wireOp",EDGE,"E17")]});Q8=makeQuery(id+"F1.opExtrude","CAP_EDGE",EDGE,{"disambiguationData":[OSD([subQ0]),TDD([makeQuery(id+"F0.imprint","IMPRINT",EDGE,{"disambiguationData":[TD([[subQ1,1.0]])],"derivedFrom":subQ0}),makeQuery(id+"F0.imprint","IMPRINT",EDGE,{"disambiguationData":[TD([[subQ1,-1.0]])],"derivedFrom":subQ0})])],"isStart":false});}
            var Q9;
            {var subQ0=sQuery(id+"F0.wireOp",EDGE,"E15");Q9=makeQuery(id+"F1.opExtrude","CAP_EDGE",EDGE,{"disambiguationData":[OSD([subQ0]),TDD([makeQuery(id+"F0.imprint","IMPRINT",EDGE,{"disambiguationData":[TD([[makeQuery(id+"F0.imprint","INTERSECT",VERTEX,{"derivedFrom":[subQ0,sQuery(id+"F0.wireOp",EDGE,"E23")]}),-1.0]])],"derivedFrom":subQ0}),makeQuery(id+"F0.imprint","IMPRINT",EDGE,{"disambiguationData":[TD([[makeQuery(id+"F0.imprint","INTERSECT",VERTEX,{"derivedFrom":[subQ0,sQuery(id+"F0.wireOp",EDGE,"E24")]}),1.0]])],"derivedFrom":subQ0})])],"isStart":false});}
            var Q10;
            {var subQ0=sQuery(id+"F0.wireOp",EDGE,"E13");var subQ1=makeQuery(id+"F0.imprint","INTERSECT",VERTEX,{"derivedFrom":[subQ0,sQuery(id+"F0.wireOp",EDGE,"E18")]});Q10=makeQuery(id+"F1.opExtrude","CAP_EDGE",EDGE,{"disambiguationData":[OSD([subQ0]),TDD([makeQuery(id+"F0.imprint","IMPRINT",EDGE,{"disambiguationData":[TD([[makeQuery(id+"F0.imprint","INTERSECT",VERTEX,{"derivedFrom":[subQ0,sQuery(id+"F0.wireOp",EDGE,"E21")]}),-1.0]])],"derivedFrom":subQ0}),makeQuery(id+"F0.imprint","IMPRINT",EDGE,{"disambiguationData":[TD([[subQ1,-1.0]])],"derivedFrom":subQ0})])],"isStart":false});}
            var Q11;
            {var subQ0=sQuery(id+"F0.wireOp",EDGE,"E16");var subQ1=makeQuery(id+"F0.imprint","INTERSECT",VERTEX,{"derivedFrom":[subQ0,sQuery(id+"F0.wireOp",EDGE,"E19")]});Q11=makeQuery(id+"F1.opExtrude","CAP_EDGE",EDGE,{"disambiguationData":[OSD([subQ0]),TDD([makeQuery(id+"F0.imprint","IMPRINT",EDGE,{"disambiguationData":[TD([[makeQuery(id+"F0.imprint","INTERSECT",VERTEX,{"derivedFrom":[subQ0,sQuery(id+"F0.wireOp",EDGE,"E24")]}),-1.0]])],"derivedFrom":subQ0}),makeQuery(id+"F0.imprint","IMPRINT",EDGE,{"disambiguationData":[TD([[subQ1,-1.0]])],"derivedFrom":subQ0})])],"isStart":false});}
            var Q12;
            {var subQ0=sQuery(id+"F0.wireOp",EDGE,"E11");var subQ1=makeQuery(id+"F0.imprint","INTERSECT",VERTEX,{"derivedFrom":[subQ0,sQuery(id+"F0.wireOp",EDGE,"E28")]});Q12=makeQuery(id+"F1.opExtrude","CAP_EDGE",EDGE,{"disambiguationData":[OSD([subQ0]),TDD([makeQuery(id+"F0.imprint","IMPRINT",EDGE,{"disambiguationData":[TD([[subQ1,1.0]])],"derivedFrom":subQ0}),makeQuery(id+"F0.imprint","IMPRINT",EDGE,{"disambiguationData":[TD([[subQ1,-1.0]])],"derivedFrom":subQ0})])],"isStart":true});}
            var Q13;
            {var subQ0=sQuery(id+"F0.wireOp",EDGE,"E10");var subQ1=makeQuery(id+"F0.imprint","INTERSECT",VERTEX,{"derivedFrom":[subQ0,sQuery(id+"F0.wireOp",EDGE,"E28")]});Q13=makeQuery(id+"F1.opExtrude","CAP_EDGE",EDGE,{"disambiguationData":[OSD([subQ0]),TDD([makeQuery(id+"F0.imprint","IMPRINT",EDGE,{"disambiguationData":[TD([[makeQuery(id+"F0.imprint","INTERSECT",VERTEX,{"disambiguationData":[OD(1.0)],"derivedFrom":[subQ0,sQuery(id+"F0.wireOp",EDGE,"E14")]}),-1.0]])],"derivedFrom":subQ0}),makeQuery(id+"F0.imprint","IMPRINT",EDGE,{"disambiguationData":[TD([[subQ1,-1.0]])],"derivedFrom":subQ0})])],"isStart":true});}
            var Q14;
            {var subQ0=sQuery(id+"F0.wireOp",EDGE,"E13");var subQ1=makeQuery(id+"F0.imprint","INTERSECT",VERTEX,{"derivedFrom":[subQ0,sQuery(id+"F0.wireOp",EDGE,"E18")]});Q14=makeQuery(id+"F1.opExtrude","CAP_EDGE",EDGE,{"disambiguationData":[OSD([subQ0]),TDD([makeQuery(id+"F0.imprint","IMPRINT",EDGE,{"disambiguationData":[TD([[makeQuery(id+"F0.imprint","INTERSECT",VERTEX,{"derivedFrom":[subQ0,sQuery(id+"F0.wireOp",EDGE,"E21")]}),-1.0]])],"derivedFrom":subQ0}),makeQuery(id+"F0.imprint","IMPRINT",EDGE,{"disambiguationData":[TD([[subQ1,-1.0]])],"derivedFrom":subQ0})])],"isStart":true});}
            var Q15;
            {var subQ0=sQuery(id+"F0.wireOp",EDGE,"E11");var subQ1=makeQuery(id+"F0.imprint","INTERSECT",VERTEX,{"derivedFrom":[subQ0,sQuery(id+"F0.wireOp",EDGE,"E27")]});Q15=makeQuery(id+"F1.opExtrude","CAP_EDGE",EDGE,{"disambiguationData":[OSD([subQ0]),TDD([makeQuery(id+"F0.imprint","IMPRINT",EDGE,{"disambiguationData":[TD([[makeQuery(id+"F0.imprint","INTERSECT",VERTEX,{"disambiguationData":[OD(1.0)],"derivedFrom":[subQ0,sQuery(id+"F0.wireOp",EDGE,"E13")]}),-1.0]])],"derivedFrom":subQ0}),makeQuery(id+"F0.imprint","IMPRINT",EDGE,{"disambiguationData":[TD([[subQ1,-1.0]])],"derivedFrom":subQ0})])],"isStart":true});}
            var Q16;
            {var subQ0=sQuery(id+"F0.wireOp",EDGE,"E12");var subQ1=makeQuery(id+"F0.imprint","INTERSECT",VERTEX,{"derivedFrom":[subQ0,sQuery(id+"F0.wireOp",EDGE,"E27")]});Q16=makeQuery(id+"F1.opExtrude","CAP_EDGE",EDGE,{"disambiguationData":[OSD([subQ0]),TDD([makeQuery(id+"F0.imprint","IMPRINT",EDGE,{"disambiguationData":[TD([[subQ1,1.0]])],"derivedFrom":subQ0}),makeQuery(id+"F0.imprint","IMPRINT",EDGE,{"disambiguationData":[TD([[subQ1,-1.0]])],"derivedFrom":subQ0})])],"isStart":true});}
            var Q17;
            {var subQ0=sQuery(id+"F0.wireOp",EDGE,"E12");var subQ1=makeQuery(id+"F0.imprint","INTERSECT",VERTEX,{"derivedFrom":[subQ0,sQuery(id+"F0.wireOp",EDGE,"E26")]});Q17=makeQuery(id+"F1.opExtrude","CAP_EDGE",EDGE,{"disambiguationData":[OSD([subQ0]),TDD([makeQuery(id+"F0.imprint","IMPRINT",EDGE,{"disambiguationData":[TD([[makeQuery(id+"F0.imprint","INTERSECT",VERTEX,{"disambiguationData":[OD(1.0)],"derivedFrom":[subQ0,sQuery(id+"F0.wireOp",EDGE,"E16")]}),-1.0]])],"derivedFrom":subQ0}),makeQuery(id+"F0.imprint","IMPRINT",EDGE,{"disambiguationData":[TD([[subQ1,-1.0]])],"derivedFrom":subQ0})])],"isStart":true});}
            var Q18;
            {var subQ0=sQuery(id+"F0.wireOp",EDGE,"E9");var subQ1=makeQuery(id+"F0.imprint","INTERSECT",VERTEX,{"derivedFrom":[subQ0,sQuery(id+"F0.wireOp",EDGE,"E26")]});Q18=makeQuery(id+"F1.opExtrude","CAP_EDGE",EDGE,{"disambiguationData":[OSD([subQ0]),TDD([makeQuery(id+"F0.imprint","IMPRINT",EDGE,{"disambiguationData":[TD([[subQ1,1.0]])],"derivedFrom":subQ0}),makeQuery(id+"F0.imprint","IMPRINT",EDGE,{"disambiguationData":[TD([[subQ1,-1.0]])],"derivedFrom":subQ0})])],"isStart":true});}
            var Q19;
            {var subQ0=sQuery(id+"F0.wireOp",EDGE,"E15");Q19=makeQuery(id+"F1.opExtrude","CAP_EDGE",EDGE,{"disambiguationData":[OSD([subQ0]),TDD([makeQuery(id+"F0.imprint","IMPRINT",EDGE,{"disambiguationData":[TD([[makeQuery(id+"F0.imprint","INTERSECT",VERTEX,{"derivedFrom":[subQ0,sQuery(id+"F0.wireOp",EDGE,"E23")]}),-1.0]])],"derivedFrom":subQ0}),makeQuery(id+"F0.imprint","IMPRINT",EDGE,{"disambiguationData":[TD([[makeQuery(id+"F0.imprint","INTERSECT",VERTEX,{"derivedFrom":[subQ0,sQuery(id+"F0.wireOp",EDGE,"E24")]}),1.0]])],"derivedFrom":subQ0})])],"isStart":true});}
            var Q20;
            {var subQ0=sQuery(id+"F0.wireOp",EDGE,"E16");var subQ1=makeQuery(id+"F0.imprint","INTERSECT",VERTEX,{"derivedFrom":[subQ0,sQuery(id+"F0.wireOp",EDGE,"E19")]});Q20=makeQuery(id+"F1.opExtrude","CAP_EDGE",EDGE,{"disambiguationData":[OSD([subQ0]),TDD([makeQuery(id+"F0.imprint","IMPRINT",EDGE,{"disambiguationData":[TD([[makeQuery(id+"F0.imprint","INTERSECT",VERTEX,{"derivedFrom":[subQ0,sQuery(id+"F0.wireOp",EDGE,"E24")]}),-1.0]])],"derivedFrom":subQ0}),makeQuery(id+"F0.imprint","IMPRINT",EDGE,{"disambiguationData":[TD([[subQ1,-1.0]])],"derivedFrom":subQ0})])],"isStart":true});}
            var Q21;
            {var subQ0=sQuery(id+"F0.wireOp",EDGE,"E9");var subQ1=makeQuery(id+"F0.imprint","INTERSECT",VERTEX,{"derivedFrom":[subQ0,sQuery(id+"F0.wireOp",EDGE,"E25")]});Q21=makeQuery(id+"F1.opExtrude","CAP_EDGE",EDGE,{"disambiguationData":[OSD([subQ0]),TDD([makeQuery(id+"F0.imprint","IMPRINT",EDGE,{"disambiguationData":[TD([[makeQuery(id+"F0.imprint","INTERSECT",VERTEX,{"disambiguationData":[OD(1.0)],"derivedFrom":[subQ0,sQuery(id+"F0.wireOp",EDGE,"E15")]}),-1.0]])],"derivedFrom":subQ0}),makeQuery(id+"F0.imprint","IMPRINT",EDGE,{"disambiguationData":[TD([[subQ1,-1.0]])],"derivedFrom":subQ0})])],"isStart":true});}
            var Q22;
            {var subQ0=sQuery(id+"F0.wireOp",EDGE,"E10");var subQ1=makeQuery(id+"F0.imprint","INTERSECT",VERTEX,{"derivedFrom":[subQ0,sQuery(id+"F0.wireOp",EDGE,"E25")]});Q22=makeQuery(id+"F1.opExtrude","CAP_EDGE",EDGE,{"disambiguationData":[OSD([subQ0]),TDD([makeQuery(id+"F0.imprint","IMPRINT",EDGE,{"disambiguationData":[TD([[subQ1,1.0]])],"derivedFrom":subQ0}),makeQuery(id+"F0.imprint","IMPRINT",EDGE,{"disambiguationData":[TD([[subQ1,-1.0]])],"derivedFrom":subQ0})])],"isStart":true});}
            var Q23;
            {var subQ0=sQuery(id+"F0.wireOp",EDGE,"E14");var subQ1=makeQuery(id+"F0.imprint","INTERSECT",VERTEX,{"derivedFrom":[subQ0,sQuery(id+"F0.wireOp",EDGE,"E17")]});Q23=makeQuery(id+"F1.opExtrude","CAP_EDGE",EDGE,{"disambiguationData":[OSD([subQ0]),TDD([makeQuery(id+"F0.imprint","IMPRINT",EDGE,{"disambiguationData":[TD([[subQ1,1.0]])],"derivedFrom":subQ0}),makeQuery(id+"F0.imprint","IMPRINT",EDGE,{"disambiguationData":[TD([[subQ1,-1.0]])],"derivedFrom":subQ0})])],"isStart":true});}
            fillet(context, id + "F4", {"entities" : qUnion([Q0, Q1, Q2, Q3, Q4, Q5, Q6, Q7, Q8, Q9, Q10, Q11, Q12, Q13, Q14, Q15, Q16, Q17, Q18, Q19, Q20, Q21, Q22, Q23]), "radius" : 1.27 * mm, "tangentPropagation" : true, "allowEdgeOverflow" : false});
        }
        {
            var Q0;
            {var subQ0=sQuery(id+"F0.wireOp",EDGE,"E15");Q0=makeQuery(id+"F2.opShell","OFFSET_EDGE",EDGE,{"disambiguationData":[OSD([subQ0]),TDD([makeQuery(id+"F1.opExtrude","CAP_EDGE",EDGE,{"disambiguationData":[OSD([subQ0]),TDD([makeQuery(id+"F0.imprint","IMPRINT",EDGE,{"disambiguationData":[TD([[makeQuery(id+"F0.imprint","INTERSECT",VERTEX,{"derivedFrom":[subQ0,sQuery(id+"F0.wireOp",EDGE,"E23")]}),-1.0]])],"derivedFrom":subQ0}),makeQuery(id+"F0.imprint","IMPRINT",EDGE,{"disambiguationData":[TD([[makeQuery(id+"F0.imprint","INTERSECT",VERTEX,{"derivedFrom":[subQ0,sQuery(id+"F0.wireOp",EDGE,"E24")]}),1.0]])],"derivedFrom":subQ0})])],"isStart":false})])]});}
            var Q1;
            {var subQ0=sQuery(id+"F0.wireOp",EDGE,"E5");Q1=makeQuery(id+"F2.opShell","OFFSET_EDGE",EDGE,{"disambiguationData":[OSD([subQ0]),TDD([makeQuery(id+"F1.opExtrude","CAP_EDGE",EDGE,{"disambiguationData":[OSD([subQ0])],"isStart":false})]),OD(1.0)]});}
            var Q2;
            {var subQ0=sQuery(id+"F0.wireOp",EDGE,"E0");Q2=makeQuery(id+"F2.opShell","OFFSET_EDGE",EDGE,{"disambiguationData":[OSD([subQ0]),TDD([makeQuery(id+"F1.opExtrude","CAP_EDGE",EDGE,{"disambiguationData":[OSD([subQ0])],"isStart":false})]),OD(1.0)]});}
            var Q3;
            {var subQ0=sQuery(id+"F0.wireOp",EDGE,"E6");Q3=makeQuery(id+"F2.opShell","OFFSET_EDGE",EDGE,{"disambiguationData":[OSD([subQ0]),TDD([makeQuery(id+"F1.opExtrude","CAP_EDGE",EDGE,{"disambiguationData":[OSD([subQ0])],"isStart":false})]),OD(0.0)]});}
            var Q4;
            {var subQ0=sQuery(id+"F0.wireOp",EDGE,"E16");var subQ1=makeQuery(id+"F0.imprint","INTERSECT",VERTEX,{"derivedFrom":[subQ0,sQuery(id+"F0.wireOp",EDGE,"E19")]});Q4=makeQuery(id+"F2.opShell","OFFSET_EDGE",EDGE,{"disambiguationData":[OSD([subQ0]),TDD([makeQuery(id+"F1.opExtrude","CAP_EDGE",EDGE,{"disambiguationData":[OSD([subQ0]),TDD([makeQuery(id+"F0.imprint","IMPRINT",EDGE,{"disambiguationData":[TD([[makeQuery(id+"F0.imprint","INTERSECT",VERTEX,{"derivedFrom":[subQ0,sQuery(id+"F0.wireOp",EDGE,"E24")]}),-1.0]])],"derivedFrom":subQ0}),makeQuery(id+"F0.imprint","IMPRINT",EDGE,{"disambiguationData":[TD([[subQ1,-1.0]])],"derivedFrom":subQ0})])],"isStart":false})])]});}
            var Q5;
            {var subQ0=sQuery(id+"F0.wireOp",EDGE,"E6");Q5=makeQuery(id+"F2.opShell","OFFSET_EDGE",EDGE,{"disambiguationData":[OSD([subQ0]),TDD([makeQuery(id+"F1.opExtrude","CAP_EDGE",EDGE,{"disambiguationData":[OSD([subQ0])],"isStart":false})]),OD(1.0)]});}
            var Q6;
            {var subQ0=sQuery(id+"F0.wireOp",EDGE,"E0");Q6=makeQuery(id+"F2.opShell","OFFSET_EDGE",EDGE,{"disambiguationData":[OSD([subQ0]),TDD([makeQuery(id+"F1.opExtrude","CAP_EDGE",EDGE,{"disambiguationData":[OSD([subQ0])],"isStart":false})]),OD(2.0)]});}
            var Q7;
            {var subQ0=sQuery(id+"F0.wireOp",EDGE,"E7");Q7=makeQuery(id+"F2.opShell","OFFSET_EDGE",EDGE,{"disambiguationData":[OSD([subQ0]),TDD([makeQuery(id+"F1.opExtrude","CAP_EDGE",EDGE,{"disambiguationData":[OSD([subQ0])],"isStart":false})]),OD(1.0)]});}
            var Q8;
            {var subQ0=sQuery(id+"F0.wireOp",EDGE,"E7");Q8=makeQuery(id+"F2.opShell","OFFSET_EDGE",EDGE,{"disambiguationData":[OSD([subQ0]),TDD([makeQuery(id+"F1.opExtrude","CAP_EDGE",EDGE,{"disambiguationData":[OSD([subQ0])],"isStart":false})]),OD(0.0)]});}
            var Q9;
            {var subQ0=sQuery(id+"F0.wireOp",EDGE,"E0");Q9=makeQuery(id+"F2.opShell","OFFSET_EDGE",EDGE,{"disambiguationData":[OSD([subQ0]),TDD([makeQuery(id+"F1.opExtrude","CAP_EDGE",EDGE,{"disambiguationData":[OSD([subQ0])],"isStart":false})]),OD(3.0)]});}
            var Q10;
            {var subQ0=sQuery(id+"F0.wireOp",EDGE,"E8");Q10=makeQuery(id+"F2.opShell","OFFSET_EDGE",EDGE,{"disambiguationData":[OSD([subQ0]),TDD([makeQuery(id+"F1.opExtrude","CAP_EDGE",EDGE,{"disambiguationData":[OSD([subQ0])],"isStart":false})]),OD(0.0)]});}
            var Q11;
            {var subQ0=sQuery(id+"F0.wireOp",EDGE,"E13");var subQ1=makeQuery(id+"F0.imprint","INTERSECT",VERTEX,{"derivedFrom":[subQ0,sQuery(id+"F0.wireOp",EDGE,"E18")]});Q11=makeQuery(id+"F2.opShell","OFFSET_EDGE",EDGE,{"disambiguationData":[OSD([subQ0]),TDD([makeQuery(id+"F1.opExtrude","CAP_EDGE",EDGE,{"disambiguationData":[OSD([subQ0]),TDD([makeQuery(id+"F0.imprint","IMPRINT",EDGE,{"disambiguationData":[TD([[makeQuery(id+"F0.imprint","INTERSECT",VERTEX,{"derivedFrom":[subQ0,sQuery(id+"F0.wireOp",EDGE,"E21")]}),-1.0]])],"derivedFrom":subQ0}),makeQuery(id+"F0.imprint","IMPRINT",EDGE,{"disambiguationData":[TD([[subQ1,-1.0]])],"derivedFrom":subQ0})])],"isStart":false})])]});}
            var Q12;
            {var subQ0=sQuery(id+"F0.wireOp",EDGE,"E8");Q12=makeQuery(id+"F2.opShell","OFFSET_EDGE",EDGE,{"disambiguationData":[OSD([subQ0]),TDD([makeQuery(id+"F1.opExtrude","CAP_EDGE",EDGE,{"disambiguationData":[OSD([subQ0])],"isStart":false})]),OD(1.0)]});}
            var Q13;
            {var subQ0=sQuery(id+"F0.wireOp",EDGE,"E0");Q13=makeQuery(id+"F2.opShell","OFFSET_EDGE",EDGE,{"disambiguationData":[OSD([subQ0]),TDD([makeQuery(id+"F1.opExtrude","CAP_EDGE",EDGE,{"disambiguationData":[OSD([subQ0])],"isStart":false})]),OD(0.0)]});}
            var Q14;
            {var subQ0=sQuery(id+"F0.wireOp",EDGE,"E14");var subQ1=makeQuery(id+"F0.imprint","INTERSECT",VERTEX,{"derivedFrom":[subQ0,sQuery(id+"F0.wireOp",EDGE,"E17")]});Q14=makeQuery(id+"F2.opShell","OFFSET_EDGE",EDGE,{"disambiguationData":[OSD([subQ0]),TDD([makeQuery(id+"F1.opExtrude","CAP_EDGE",EDGE,{"disambiguationData":[OSD([subQ0]),TDD([makeQuery(id+"F0.imprint","IMPRINT",EDGE,{"disambiguationData":[TD([[subQ1,1.0]])],"derivedFrom":subQ0}),makeQuery(id+"F0.imprint","IMPRINT",EDGE,{"disambiguationData":[TD([[subQ1,-1.0]])],"derivedFrom":subQ0})])],"isStart":false})])]});}
            var Q15;
            {var subQ0=sQuery(id+"F0.wireOp",EDGE,"E5");Q15=makeQuery(id+"F2.opShell","OFFSET_EDGE",EDGE,{"disambiguationData":[OSD([subQ0]),TDD([makeQuery(id+"F1.opExtrude","CAP_EDGE",EDGE,{"disambiguationData":[OSD([subQ0])],"isStart":false})]),OD(0.0)]});}
            chamfer(context, id + "F5", {"entities" : qUnion([Q0, Q1, Q2, Q3, Q4, Q5, Q6, Q7, Q8, Q9, Q10, Q11, Q12, Q13, Q14, Q15]), "width" : 0.5 * mm, "tangentPropagation" : true});
        }
        {
            var Q0;
            {var subQ0=sQuery(id+"F0.wireOp",EDGE,"E14");var subQ1=makeQuery(id+"F0.imprint","INTERSECT",VERTEX,{"derivedFrom":[subQ0,sQuery(id+"F0.wireOp",EDGE,"E17")]});Q0=makeQuery(id+"F2.opShell","OFFSET_EDGE",EDGE,{"disambiguationData":[OSD([subQ0]),TDD([makeQuery(id+"F1.opExtrude","CAP_EDGE",EDGE,{"disambiguationData":[OSD([subQ0]),TDD([makeQuery(id+"F0.imprint","IMPRINT",EDGE,{"disambiguationData":[TD([[subQ1,1.0]])],"derivedFrom":subQ0}),makeQuery(id+"F0.imprint","IMPRINT",EDGE,{"disambiguationData":[TD([[subQ1,-1.0]])],"derivedFrom":subQ0})])],"isStart":true})])]});}
            var Q1;
            {var subQ0=sQuery(id+"F0.wireOp",EDGE,"E8");Q1=makeQuery(id+"F2.opShell","OFFSET_EDGE",EDGE,{"disambiguationData":[OSD([subQ0]),TDD([makeQuery(id+"F1.opExtrude","CAP_EDGE",EDGE,{"disambiguationData":[OSD([subQ0])],"isStart":true})]),OD(1.0)]});}
            var Q2;
            {var subQ0=sQuery(id+"F0.wireOp",EDGE,"E0");Q2=makeQuery(id+"F2.opShell","OFFSET_EDGE",EDGE,{"disambiguationData":[OSD([subQ0]),TDD([makeQuery(id+"F1.opExtrude","CAP_EDGE",EDGE,{"disambiguationData":[OSD([subQ0])],"isStart":true})]),OD(0.0)]});}
            var Q3;
            {var subQ0=sQuery(id+"F0.wireOp",EDGE,"E5");Q3=makeQuery(id+"F2.opShell","OFFSET_EDGE",EDGE,{"disambiguationData":[OSD([subQ0]),TDD([makeQuery(id+"F1.opExtrude","CAP_EDGE",EDGE,{"disambiguationData":[OSD([subQ0])],"isStart":true})]),OD(0.0)]});}
            var Q4;
            {var subQ0=sQuery(id+"F0.wireOp",EDGE,"E0");Q4=makeQuery(id+"F2.opShell","OFFSET_EDGE",EDGE,{"disambiguationData":[OSD([subQ0]),TDD([makeQuery(id+"F1.opExtrude","CAP_EDGE",EDGE,{"disambiguationData":[OSD([subQ0])],"isStart":true})]),OD(1.0)]});}
            var Q5;
            {var subQ0=sQuery(id+"F0.wireOp",EDGE,"E5");Q5=makeQuery(id+"F2.opShell","OFFSET_EDGE",EDGE,{"disambiguationData":[OSD([subQ0]),TDD([makeQuery(id+"F1.opExtrude","CAP_EDGE",EDGE,{"disambiguationData":[OSD([subQ0])],"isStart":true})]),OD(1.0)]});}
            var Q6;
            {var subQ0=sQuery(id+"F0.wireOp",EDGE,"E15");Q6=makeQuery(id+"F2.opShell","OFFSET_EDGE",EDGE,{"disambiguationData":[OSD([subQ0]),TDD([makeQuery(id+"F1.opExtrude","CAP_EDGE",EDGE,{"disambiguationData":[OSD([subQ0]),TDD([makeQuery(id+"F0.imprint","IMPRINT",EDGE,{"disambiguationData":[TD([[makeQuery(id+"F0.imprint","INTERSECT",VERTEX,{"derivedFrom":[subQ0,sQuery(id+"F0.wireOp",EDGE,"E23")]}),-1.0]])],"derivedFrom":subQ0}),makeQuery(id+"F0.imprint","IMPRINT",EDGE,{"disambiguationData":[TD([[makeQuery(id+"F0.imprint","INTERSECT",VERTEX,{"derivedFrom":[subQ0,sQuery(id+"F0.wireOp",EDGE,"E24")]}),1.0]])],"derivedFrom":subQ0})])],"isStart":true})])]});}
            var Q7;
            {var subQ0=sQuery(id+"F0.wireOp",EDGE,"E6");Q7=makeQuery(id+"F2.opShell","OFFSET_EDGE",EDGE,{"disambiguationData":[OSD([subQ0]),TDD([makeQuery(id+"F1.opExtrude","CAP_EDGE",EDGE,{"disambiguationData":[OSD([subQ0])],"isStart":true})]),OD(0.0)]});}
            var Q8;
            {var subQ0=sQuery(id+"F0.wireOp",EDGE,"E6");Q8=makeQuery(id+"F2.opShell","OFFSET_EDGE",EDGE,{"disambiguationData":[OSD([subQ0]),TDD([makeQuery(id+"F1.opExtrude","CAP_EDGE",EDGE,{"disambiguationData":[OSD([subQ0])],"isStart":true})]),OD(1.0)]});}
            var Q9;
            {var subQ0=sQuery(id+"F0.wireOp",EDGE,"E0");Q9=makeQuery(id+"F2.opShell","OFFSET_EDGE",EDGE,{"disambiguationData":[OSD([subQ0]),TDD([makeQuery(id+"F1.opExtrude","CAP_EDGE",EDGE,{"disambiguationData":[OSD([subQ0])],"isStart":true})]),OD(2.0)]});}
            var Q10;
            {var subQ0=sQuery(id+"F0.wireOp",EDGE,"E16");var subQ1=makeQuery(id+"F0.imprint","INTERSECT",VERTEX,{"derivedFrom":[subQ0,sQuery(id+"F0.wireOp",EDGE,"E19")]});Q10=makeQuery(id+"F2.opShell","OFFSET_EDGE",EDGE,{"disambiguationData":[OSD([subQ0]),TDD([makeQuery(id+"F1.opExtrude","CAP_EDGE",EDGE,{"disambiguationData":[OSD([subQ0]),TDD([makeQuery(id+"F0.imprint","IMPRINT",EDGE,{"disambiguationData":[TD([[makeQuery(id+"F0.imprint","INTERSECT",VERTEX,{"derivedFrom":[subQ0,sQuery(id+"F0.wireOp",EDGE,"E24")]}),-1.0]])],"derivedFrom":subQ0}),makeQuery(id+"F0.imprint","IMPRINT",EDGE,{"disambiguationData":[TD([[subQ1,-1.0]])],"derivedFrom":subQ0})])],"isStart":true})])]});}
            var Q11;
            {var subQ0=sQuery(id+"F0.wireOp",EDGE,"E7");Q11=makeQuery(id+"F2.opShell","OFFSET_EDGE",EDGE,{"disambiguationData":[OSD([subQ0]),TDD([makeQuery(id+"F1.opExtrude","CAP_EDGE",EDGE,{"disambiguationData":[OSD([subQ0])],"isStart":true})]),OD(1.0)]});}
            var Q12;
            {var subQ0=sQuery(id+"F0.wireOp",EDGE,"E7");Q12=makeQuery(id+"F2.opShell","OFFSET_EDGE",EDGE,{"disambiguationData":[OSD([subQ0]),TDD([makeQuery(id+"F1.opExtrude","CAP_EDGE",EDGE,{"disambiguationData":[OSD([subQ0])],"isStart":true})]),OD(0.0)]});}
            var Q13;
            {var subQ0=sQuery(id+"F0.wireOp",EDGE,"E13");var subQ1=makeQuery(id+"F0.imprint","INTERSECT",VERTEX,{"derivedFrom":[subQ0,sQuery(id+"F0.wireOp",EDGE,"E18")]});Q13=makeQuery(id+"F2.opShell","OFFSET_EDGE",EDGE,{"disambiguationData":[OSD([subQ0]),TDD([makeQuery(id+"F1.opExtrude","CAP_EDGE",EDGE,{"disambiguationData":[OSD([subQ0]),TDD([makeQuery(id+"F0.imprint","IMPRINT",EDGE,{"disambiguationData":[TD([[makeQuery(id+"F0.imprint","INTERSECT",VERTEX,{"derivedFrom":[subQ0,sQuery(id+"F0.wireOp",EDGE,"E21")]}),-1.0]])],"derivedFrom":subQ0}),makeQuery(id+"F0.imprint","IMPRINT",EDGE,{"disambiguationData":[TD([[subQ1,-1.0]])],"derivedFrom":subQ0})])],"isStart":true})])]});}
            var Q14;
            {var subQ0=sQuery(id+"F0.wireOp",EDGE,"E8");Q14=makeQuery(id+"F2.opShell","OFFSET_EDGE",EDGE,{"disambiguationData":[OSD([subQ0]),TDD([makeQuery(id+"F1.opExtrude","CAP_EDGE",EDGE,{"disambiguationData":[OSD([subQ0])],"isStart":true})]),OD(0.0)]});}
            var Q15;
            {var subQ0=sQuery(id+"F0.wireOp",EDGE,"E0");Q15=makeQuery(id+"F2.opShell","OFFSET_EDGE",EDGE,{"disambiguationData":[OSD([subQ0]),TDD([makeQuery(id+"F1.opExtrude","CAP_EDGE",EDGE,{"disambiguationData":[OSD([subQ0])],"isStart":true})]),OD(3.0)]});}
            chamfer(context, id + "F6", {"entities" : qUnion([Q0, Q1, Q2, Q3, Q4, Q5, Q6, Q7, Q8, Q9, Q10, Q11, Q12, Q13, Q14, Q15]), "width" : 0.5 * mm, "tangentPropagation" : true});
        }
    });
